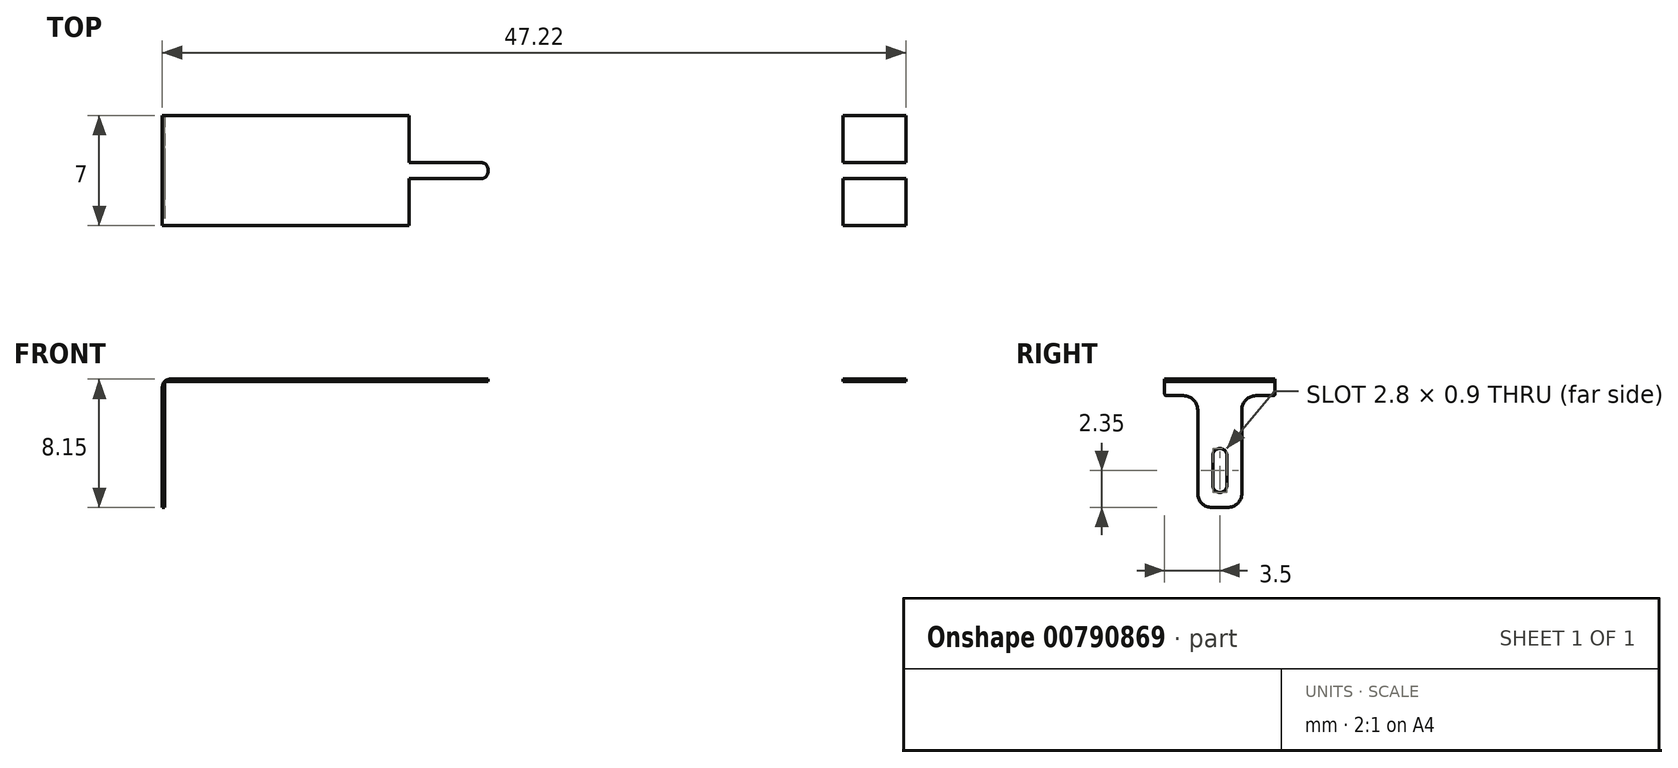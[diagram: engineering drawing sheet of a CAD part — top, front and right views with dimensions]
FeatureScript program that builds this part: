
annotation { "Feature Type Name" : "Feature", "Feature Type Description" : "" }
export const myFeature = defineFeature(function(context is Context, id is Id, definition is map)
    precondition{}
    {
        {
            var Q0;
            Q0=qCreatedBy(makeId("Top.planeOp"),FACE);
            var sketch = newSketch(context, id + "F0", { "sketchPlane" : qUnion([Q0])});
            skPoint(sketch, "E0.middle", {"position": v(0, 0) * mm});
            skLineSegment(sketch, "E1.bottom", {"start": v(-9.18, -0.5) * mm, "end": v(-13.77, -0.5) * mm});
            skLineSegment(sketch, "E1.top", {"start": v(-9.18, 0.5) * mm, "end": v(-13.77, 0.5) * mm});
            skLineSegment(sketch, "E1.left", {"start": v(-8.78, -0.1) * mm, "end": v(-8.78, 0.1) * mm});
            skLineSegment(sketch, "E1.right", {"start": v(-18.78, -0.1) * mm, "end": v(-18.78, 0.1) * mm});
            skPoint(sketch, "E1.middle", {"position": v(-13.78, 0) * mm});
            skPoint(sketch, "E2.visualSharp", {"position": v(-8.78, 0.5) * mm});
            skArc(sketch, "E2.filletArc", {"start": v(-8.78, 0.1) * mm, "mid": v(-8.9, 0.38) * mm, "end": v(-9.18, 0.5) * mm});
            skPoint(sketch, "E3.visualSharp", {"position": v(-8.78, -0.5) * mm});
            skArc(sketch, "E3.filletArc", {"start": v(-9.18, -0.5) * mm, "mid": v(-8.9, -0.38) * mm, "end": v(-8.78, -0.1) * mm});
            skPoint(sketch, "E4.visualSharp", {"position": v(-18.78, 0.5) * mm});
            skArc(sketch, "E4.filletArc", {"start": v(-18.38, 0.5) * mm, "mid": v(-18.66, 0.38) * mm, "end": v(-18.77, 0.1) * mm});
            skPoint(sketch, "E5.visualSharp", {"position": v(-18.78, -0.5) * mm});
            skArc(sketch, "E5.filletArc", {"start": v(-18.77, -0.1) * mm, "mid": v(-18.66, -0.38) * mm, "end": v(-18.38, -0.5) * mm});
            skLineSegment(sketch, "E6", {"start": v(0, 3.5) * mm, "end": v(-13.78, 3.5) * mm});
            skPoint(sketch, "E6.endSnap0", {"position": v(-13.77, 0.5) * mm});
            skLineSegment(sketch, "E7", {"start": v(-13.78, 3.5) * mm, "end": v(-13.78, 0.5) * mm});
            skLineSegment(sketch, "E8.MirrorCS", {"start": v(0, -3.5) * mm, "end": v(-13.78, -3.5) * mm});
            skLineSegment(sketch, "E9.MirrorCS", {"start": v(-13.78, -3.5) * mm, "end": v(-13.78, -0.5) * mm});
            skLineSegment(sketch, "E10.MirrorCS", {"start": v(0, 3.5) * mm, "end": v(13.78, 3.5) * mm});
            skLineSegment(sketch, "E11.MirrorCS", {"start": v(0, -3.5) * mm, "end": v(13.78, -3.5) * mm});
            skLineSegment(sketch, "E12.MirrorCS", {"start": v(8.78, -0.1) * mm, "end": v(8.78, 0.1) * mm});
            skArc(sketch, "E13.MirrorCS", {"start": v(8.78, 0.1) * mm, "mid": v(8.9, 0.38) * mm, "end": v(9.18, 0.5) * mm});
            skArc(sketch, "E14.MirrorCS", {"start": v(18.77, -0.1) * mm, "mid": v(18.66, -0.38) * mm, "end": v(18.38, -0.5) * mm});
            skLineSegment(sketch, "E15.MirrorCS", {"start": v(18.78, -0.1) * mm, "end": v(18.78, 0.1) * mm});
            skArc(sketch, "E16.MirrorCS", {"start": v(18.38, 0.5) * mm, "mid": v(18.66, 0.38) * mm, "end": v(18.77, 0.1) * mm});
            skArc(sketch, "E17.MirrorCS", {"start": v(9.18, -0.5) * mm, "mid": v(8.9, -0.38) * mm, "end": v(8.78, -0.1) * mm});
            skPoint(sketch, "E18.MirrorP", {"position": v(18.78, 0.5) * mm});
            skLineSegment(sketch, "E19.MirrorCS", {"start": v(9.18, 0.5) * mm, "end": v(18.38, 0.5) * mm});
            skLineSegment(sketch, "E20.MirrorCS", {"start": v(9.18, -0.5) * mm, "end": v(18.38, -0.5) * mm});
            skPoint(sketch, "E21.MirrorP", {"position": v(13.77, 0.5) * mm});
            skPoint(sketch, "E22.MirrorP", {"position": v(8.78, 0.5) * mm});
            skPoint(sketch, "E23.MirrorP", {"position": v(18.78, -0.5) * mm});
            skPoint(sketch, "E24.MirrorP", {"position": v(8.78, -0.5) * mm});
            skPoint(sketch, "E25.MirrorP", {"position": v(13.78, 0) * mm});
            skLineSegment(sketch, "E26.MirrorCS", {"start": v(13.78, 3.5) * mm, "end": v(13.78, 0.5) * mm});
            skLineSegment(sketch, "E27.MirrorCS", {"start": v(13.78, -3.5) * mm, "end": v(13.78, -0.5) * mm});
            skPoint(sketch, "E28.1.0.0", {"position": v(36.33, 0.5) * mm});
            skLineSegment(sketch, "E28.1.0.1", {"start": v(27.55, 3.5) * mm, "end": v(41.33, 3.5) * mm});
            skLineSegment(sketch, "E28.1.0.2", {"start": v(36.73, -0.5) * mm, "end": v(45.93, -0.5) * mm});
            skPoint(sketch, "E28.1.0.3", {"position": v(27.55, 0) * mm});
            skLineSegment(sketch, "E28.1.0.4", {"start": v(27.55, -3.5) * mm, "end": v(41.33, -3.5) * mm});
            skPoint(sketch, "E28.1.0.5", {"position": v(41.33, 0.5) * mm});
            skPoint(sketch, "E28.1.0.6", {"position": v(41.33, 0) * mm});
            skPoint(sketch, "E28.1.0.7", {"position": v(46.33, -0.5) * mm});
            skPoint(sketch, "E28.1.0.8", {"position": v(36.33, -0.5) * mm});
            skLineSegment(sketch, "E28.1.0.9", {"start": v(27.55, -3.5) * mm, "end": v(13.78, -3.5) * mm});
            skLineSegment(sketch, "E28.1.0.10", {"start": v(36.73, 0.5) * mm, "end": v(45.93, 0.5) * mm});
            skLineSegment(sketch, "E28.1.0.11", {"start": v(27.55, 3.5) * mm, "end": v(13.78, 3.5) * mm});
            skLineSegment(sketch, "E28.1.0.12", {"start": v(41.33, 3.5) * mm, "end": v(41.33, 0.5) * mm});
            skLineSegment(sketch, "E28.1.0.13", {"start": v(41.33, -3.5) * mm, "end": v(41.33, -0.5) * mm});
            skPoint(sketch, "E28.1.0.14", {"position": v(46.33, 0.5) * mm});
            skArc(sketch, "E28.1.0.15", {"start": v(45.93, 0.5) * mm, "mid": v(46.2, 0.38) * mm, "end": v(46.32, 0.1) * mm});
            skArc(sketch, "E28.1.0.16", {"start": v(36.73, -0.5) * mm, "mid": v(36.44, -0.38) * mm, "end": v(36.33, -0.1) * mm});
            skArc(sketch, "E28.1.0.17", {"start": v(46.33, -0.1) * mm, "mid": v(46.2, -0.38) * mm, "end": v(45.93, -0.5) * mm});
            skArc(sketch, "E28.1.0.18", {"start": v(36.33, 0.1) * mm, "mid": v(36.44, 0.38) * mm, "end": v(36.73, 0.5) * mm});
            skLineSegment(sketch, "E28.1.0.19", {"start": v(36.32, -0.1) * mm, "end": v(36.32, 0.1) * mm});
            skLineSegment(sketch, "E28.1.0.20", {"start": v(46.33, -0.1) * mm, "end": v(46.33, 0.1) * mm});
            skLineSegment(sketch, "E28.direction1", {"start": v(-13.78, -3.5) * mm, "end": v(13.78, -3.5) * mm, "construction": true});
            skLineSegment(sketch, "E29", {"start": v(0, 3.5) * mm, "end": v(0, -3.5) * mm});
            skLineSegment(sketch, "E30.bottom", {"start": v(96.43, -3.5) * mm, "end": v(99.43, -3.5) * mm});
            skLineSegment(sketch, "E30.top", {"start": v(96.43, 3.5) * mm, "end": v(99.43, 3.5) * mm});
            skLineSegment(sketch, "E30.left", {"start": v(96.43, -3.5) * mm, "end": v(96.43, 3.5) * mm});
            skLineSegment(sketch, "E31.bottom", {"start": v(41.33, -3.5) * mm, "end": v(45.33, -3.5) * mm});
            skLineSegment(sketch, "E31.top", {"start": v(41.33, 3.5) * mm, "end": v(45.33, 3.5) * mm});
            skLineSegment(sketch, "E31.left", {"start": v(41.33, -3.5) * mm, "end": v(41.33, 3.5) * mm});
            skLineSegment(sketch, "E31.right", {"start": v(45.33, -3.5) * mm, "end": v(45.33, 3.5) * mm});
            skSolve(sketch);
        }
        {
            var Q0;
            {var subQ8=sQuery(id+"F0.wireOp",EDGE,"E28.3.0.12");Q0=makeQuery(id+"F0.imprint","IMPRINT",FACE,{"disambiguationData":[TD([[makeQuery(id+"F0.imprint","IMPRINT",EDGE,{"derivedFrom":subQ8}),1.0]])]});}
            var Q1;
            {var subQ3=sQuery(id+"F0.wireOp",EDGE,"E14.MirrorCS");Q1=makeQuery(id+"F0.imprint","IMPRINT",FACE,{"disambiguationData":[TD([[makeQuery(id+"F0.imprint","IMPRINT",EDGE,{"derivedFrom":subQ3}),1.0]])]});}
            var Q2;
            {var subQ8=sQuery(id+"F0.wireOp",EDGE,"E28.1.0.12");Q2=makeQuery(id+"F0.imprint","IMPRINT",FACE,{"disambiguationData":[TD([[makeQuery(id+"F0.imprint","IMPRINT",EDGE,{"derivedFrom":subQ8}),1.0]])]});}
            var Q3;
            {var subQ8=sQuery(id+"F0.wireOp",EDGE,"E28.2.0.12");Q3=makeQuery(id+"F0.imprint","IMPRINT",FACE,{"disambiguationData":[TD([[makeQuery(id+"F0.imprint","IMPRINT",EDGE,{"derivedFrom":subQ8}),1.0]])]});}
            var Q4;
            Q4=makeQuery(id+"F0.imprint","IMPRINT",FACE,{"disambiguationData":[TD([[makeQuery(id+"F0.imprint","IMPRINT",EDGE,{"derivedFrom":sQuery(id+"F0.wireOp",EDGE,"E10.MirrorCS")}),-1.0]])]});
            var Q5;
            {var subQ5=sQuery(id+"F0.wireOp",EDGE,"E30.top");Q5=makeQuery(id+"F0.imprint","IMPRINT",FACE,{"disambiguationData":[TD([[makeQuery(id+"F0.imprint","IMPRINT",EDGE,{"derivedFrom":subQ5}),-1.0]])]});}
            var Q6;
            {var subQ5=sQuery(id+"F0.wireOp",EDGE,"E30.bottom");Q6=makeQuery(id+"F0.imprint","IMPRINT",FACE,{"disambiguationData":[TD([[makeQuery(id+"F0.imprint","IMPRINT",EDGE,{"derivedFrom":subQ5}),1.0]])]});}
            var Q7;
            {var subQ11=sQuery(id+"F0.wireOp",EDGE,"E28.3.0.15");Q7=makeQuery(id+"F0.imprint","IMPRINT",FACE,{"disambiguationData":[TD([[makeQuery(id+"F0.imprint","IMPRINT",EDGE,{"derivedFrom":subQ11}),1.0]])]});}
            var Q8;
            {var subQ5=sQuery(id+"F0.wireOp",EDGE,"E31.top");Q8=makeQuery(id+"F0.imprint","IMPRINT",FACE,{"disambiguationData":[TD([[makeQuery(id+"F0.imprint","IMPRINT",EDGE,{"derivedFrom":subQ5}),-1.0]])]});}
            var Q9;
            {var subQ5=sQuery(id+"F0.wireOp",EDGE,"E31.bottom");Q9=makeQuery(id+"F0.imprint","IMPRINT",FACE,{"disambiguationData":[TD([[makeQuery(id+"F0.imprint","IMPRINT",EDGE,{"derivedFrom":subQ5}),1.0]])]});}
            extrude(context, id + "F1", {"entities" : qUnion([Q0, Q1, Q2, Q3, Q4, Q5, Q6, Q7, Q8, Q9]), "depth" : 0.15 * mm, "offsetDistance" : 25 * mm});
        }
        {
            var Q0;
            Q0=makeQuery(id+"F1.opExtrude","SWEPT_FACE",FACE,{"disambiguationData":[OSD([sQuery(id+"F0.wireOp",EDGE,"E29")])]});
            extrude(context, id + "F2", {"entities" : qUnion([Q0]), "operationType" : NewBodyOperationType.ADD, "depth" : 1.9 * mm, "offsetDistance" : 25 * mm});
        }
        {
            var Q0;
            {var subQ0=sQuery(id+"F0.wireOp",EDGE,"E29");Q0=makeQuery(id+"F2.boolean.opBoolean","MERGE",FACE,{"derivedFrom":[makeQuery(id+"F1.opExtrude","CAP_FACE",FACE,{"disambiguationData":[OSD([sQuery(id+"F0.wireOp",EDGE,"E10.MirrorCS"),sQuery(id+"F0.wireOp",EDGE,"E11.MirrorCS"),sQuery(id+"F0.wireOp",EDGE,"E12.MirrorCS"),sQuery(id+"F0.wireOp",EDGE,"E13.MirrorCS"),sQuery(id+"F0.wireOp",EDGE,"E14.MirrorCS"),sQuery(id+"F0.wireOp",EDGE,"E15.MirrorCS"),sQuery(id+"F0.wireOp",EDGE,"E16.MirrorCS"),sQuery(id+"F0.wireOp",EDGE,"E17.MirrorCS"),sQuery(id+"F0.wireOp",EDGE,"E19.MirrorCS"),sQuery(id+"F0.wireOp",EDGE,"E20.MirrorCS"),sQuery(id+"F0.wireOp",EDGE,"E28.1.0.1"),sQuery(id+"F0.wireOp",EDGE,"E28.1.0.2"),sQuery(id+"F0.wireOp",EDGE,"E28.1.0.4"),sQuery(id+"F0.wireOp",EDGE,"E28.1.0.9"),sQuery(id+"F0.wireOp",EDGE,"E28.1.0.10"),sQuery(id+"F0.wireOp",EDGE,"E28.1.0.11"),sQuery(id+"F0.wireOp",EDGE,"E28.1.0.15"),sQuery(id+"F0.wireOp",EDGE,"E28.1.0.16"),sQuery(id+"F0.wireOp",EDGE,"E28.1.0.17"),sQuery(id+"F0.wireOp",EDGE,"E28.1.0.18"),sQuery(id+"F0.wireOp",EDGE,"E28.1.0.19"),sQuery(id+"F0.wireOp",EDGE,"E28.1.0.20"),sQuery(id+"F0.wireOp",EDGE,"E28.2.0.1"),sQuery(id+"F0.wireOp",EDGE,"E28.2.0.2"),sQuery(id+"F0.wireOp",EDGE,"E28.2.0.4"),sQuery(id+"F0.wireOp",EDGE,"E28.2.0.9"),sQuery(id+"F0.wireOp",EDGE,"E28.2.0.10"),sQuery(id+"F0.wireOp",EDGE,"E28.2.0.11"),sQuery(id+"F0.wireOp",EDGE,"E28.2.0.15"),sQuery(id+"F0.wireOp",EDGE,"E28.2.0.16"),sQuery(id+"F0.wireOp",EDGE,"E28.2.0.17"),sQuery(id+"F0.wireOp",EDGE,"E28.2.0.18"),sQuery(id+"F0.wireOp",EDGE,"E28.2.0.19"),sQuery(id+"F0.wireOp",EDGE,"E28.2.0.20"),sQuery(id+"F0.wireOp",EDGE,"E28.3.0.1"),sQuery(id+"F0.wireOp",EDGE,"E28.3.0.2"),sQuery(id+"F0.wireOp",EDGE,"E28.3.0.4"),sQuery(id+"F0.wireOp",EDGE,"E28.3.0.9"),sQuery(id+"F0.wireOp",EDGE,"E28.3.0.10"),sQuery(id+"F0.wireOp",EDGE,"E28.3.0.11"),sQuery(id+"F0.wireOp",EDGE,"E28.3.0.12"),sQuery(id+"F0.wireOp",EDGE,"E28.3.0.13"),sQuery(id+"F0.wireOp",EDGE,"E28.3.0.16"),sQuery(id+"F0.wireOp",EDGE,"E28.3.0.18"),sQuery(id+"F0.wireOp",EDGE,"E28.3.0.19"),subQ0])],"isStart":true}),makeQuery(id+"F2.opExtrude","SWEPT_FACE",FACE,{"disambiguationData":[OSD([subQ0]),TDD([makeQuery(id+"F1.opExtrude","CAP_EDGE",EDGE,{"disambiguationData":[OSD([subQ0])],"isStart":true})])]})]});}
            var sketch = newSketch(context, id + "F3", { "sketchPlane" : qUnion([Q0])});
            skLineSegment(sketch, "E32.bottom", {"start": v(-1.9, -3.5) * mm, "end": v(-1.75, -3.5) * mm});
            skLineSegment(sketch, "E32.top", {"start": v(-1.9, 3.5) * mm, "end": v(-1.75, 3.5) * mm});
            skLineSegment(sketch, "E32.left", {"start": v(-1.9, -3.5) * mm, "end": v(-1.9, 3.5) * mm});
            skLineSegment(sketch, "E32.right", {"start": v(-1.75, -3.5) * mm, "end": v(-1.75, 3.5) * mm});
            skSolve(sketch);
        }
        {
            var Q0;
            Q0=qSketchRegion(id+"F3",true);
            extrude(context, id + "F4", {"entities" : qUnion([Q0]), "operationType" : NewBodyOperationType.ADD, "depth" : 8 * mm, "offsetDistance" : 25 * mm});
        }
        {
            var Q0;
            Q0=makeQuery(id+"F4.boolean.opBoolean","MERGE",FACE,{"derivedFrom":[makeQuery(id+"F2.opExtrude","CAP_FACE",FACE,{"disambiguationData":[OSD([sQuery(id+"F0.wireOp",EDGE,"E29")])],"isStart":false}),makeQuery(id+"F4.opExtrude","SWEPT_FACE",FACE,{"disambiguationData":[OSD([sQuery(id+"F3.wireOp",EDGE,"E32.left")])]})]});
            var sketch = newSketch(context, id + "F5", { "sketchPlane" : qUnion([Q0])});
            skPoint(sketch, "E33.middle.positionSnap0", {"position": v(0, -8) * mm});
            skLineSegment(sketch, "E34.bottom", {"start": v(-0.5, -8) * mm, "end": v(0.5, -8) * mm});
            skLineSegment(sketch, "E34.top", {"start": v(-1.4, -0.9) * mm, "end": v(1.4, -0.9) * mm});
            skLineSegment(sketch, "E34.left", {"start": v(-1.4, -7.1) * mm, "end": v(-1.4, -1.8) * mm});
            skLineSegment(sketch, "E34.right", {"start": v(1.4, -7.1) * mm, "end": v(1.4, -1.8) * mm});
            skLineSegment(sketch, "E35", {"start": v(2.3, -0.9) * mm, "end": v(3.4, -0.9) * mm});
            skLineSegment(sketch, "E36", {"start": v(-2.3, -0.9) * mm, "end": v(-3.4, -0.9) * mm});
            skCircle(sketch, "E37", {"center": v(0, -6.6) * mm, "radius": 0.45 * mm});
            skCircle(sketch, "E38", {"center": v(0, -4.7) * mm, "radius": 0.45 * mm});
            skLineSegment(sketch, "E39", {"start": v(0.45, -4.7) * mm, "end": v(0.45, -6.6) * mm});
            skLineSegment(sketch, "E40", {"start": v(-0.45, -4.7) * mm, "end": v(-0.45, -6.6) * mm});
            skPoint(sketch, "E41.visualSharp", {"position": v(-1.4, -8) * mm});
            skArc(sketch, "E41.filletArc", {"start": v(-1.4, -7.1) * mm, "mid": v(-1.14, -7.74) * mm, "end": v(-0.5, -8) * mm});
            skPoint(sketch, "E42.visualSharp", {"position": v(1.4, -8) * mm});
            skArc(sketch, "E42.filletArc", {"start": v(0.5, -8) * mm, "mid": v(1.14, -7.74) * mm, "end": v(1.4, -7.1) * mm});
            skPoint(sketch, "E43.visualSharp", {"position": v(-1.4, -0.9) * mm});
            skArc(sketch, "E43.filletArc", {"start": v(-1.4, -1.8) * mm, "mid": v(-1.66, -1.16) * mm, "end": v(-2.3, -0.9) * mm});
            skPoint(sketch, "E44.visualSharp", {"position": v(1.4, -0.9) * mm});
            skArc(sketch, "E44.filletArc", {"start": v(2.3, -0.9) * mm, "mid": v(1.66, -1.16) * mm, "end": v(1.4, -1.8) * mm});
            skLineSegment(sketch, "E45", {"start": v(-3.5, -0.8) * mm, "end": v(-3.5, 0.15) * mm});
            skLineSegment(sketch, "E46", {"start": v(3.5, -0.8) * mm, "end": v(3.5, 0.15) * mm});
            skPoint(sketch, "E47.visualSharp", {"position": v(-3.5, -0.9) * mm});
            skArc(sketch, "E47.filletArc", {"start": v(-3.5, -0.8) * mm, "mid": v(-3.47, -0.87) * mm, "end": v(-3.4, -0.9) * mm});
            skPoint(sketch, "E48.visualSharp", {"position": v(3.5, -0.9) * mm});
            skArc(sketch, "E48.filletArc", {"start": v(3.4, -0.9) * mm, "mid": v(3.47, -0.87) * mm, "end": v(3.5, -0.8) * mm});
            skSolve(sketch);
        }
        {
            var Q0;
            Q0=makeQuery(id+"F5.imprint","IMPRINT",FACE,{"disambiguationData":[TD([[makeQuery(id+"F5.imprint","IMPRINT",EDGE,{"derivedFrom":sQuery(id+"F5.wireOp",EDGE,"E34.left")}),1.0]])]});
            var Q1;
            Q1=makeQuery(id+"F5.imprint","IMPRINT",FACE,{"disambiguationData":[TD([[makeQuery(id+"F5.imprint","IMPRINT",EDGE,{"derivedFrom":sQuery(id+"F5.wireOp",EDGE,"E34.right")}),-1.0]])]});
            var Q2;
            {var subQ0=sQuery(id+"F5.wireOp",EDGE,"E37");var subQ1=makeQuery(id+"F5.imprint","INTERSECT",VERTEX,{"derivedFrom":[subQ0,sQuery(id+"F5.wireOp",EDGE,"E39")]});Q2=makeQuery(id+"F5.imprint","IMPRINT",FACE,{"disambiguationData":[TD([[makeQuery(id+"F5.imprint","IMPRINT",EDGE,{"disambiguationData":[TD([[subQ1,-1.0]])],"derivedFrom":subQ0}),1.0]])]});}
            var Q3;
            {var subQ0=sQuery(id+"F5.wireOp",EDGE,"E39");Q3=makeQuery(id+"F5.imprint","IMPRINT",FACE,{"disambiguationData":[TD([[makeQuery(id+"F5.imprint","IMPRINT",EDGE,{"derivedFrom":subQ0}),-1.0]])]});}
            var Q4;
            {var subQ0=sQuery(id+"F5.wireOp",EDGE,"E38");var subQ1=makeQuery(id+"F5.imprint","INTERSECT",VERTEX,{"derivedFrom":[subQ0,sQuery(id+"F5.wireOp",EDGE,"E39")]});Q4=makeQuery(id+"F5.imprint","IMPRINT",FACE,{"disambiguationData":[TD([[makeQuery(id+"F5.imprint","IMPRINT",EDGE,{"disambiguationData":[TD([[subQ1,-1.0]])],"derivedFrom":subQ0}),1.0]])]});}
            extrude(context, id + "F6", {"entities" : qUnion([Q0, Q1, Q2, Q3, Q4]), "operationType" : NewBodyOperationType.REMOVE, "oppositeDirection" : true, "depth" : 25 * mm, "offsetDistance" : 25 * mm});
        }
        {
            var Q0;
            {var subQ0=sQuery(id+"F0.wireOp",EDGE,"E29");Q0=makeQuery(id+"F2.opExtrude","CAP_EDGE",EDGE,{"disambiguationData":[OSD([subQ0]),TDD([makeQuery(id+"F1.opExtrude","CAP_EDGE",EDGE,{"disambiguationData":[OSD([subQ0])],"isStart":false})])],"isStart":false});}
            var Q1;
            Q1=makeQuery(id+"F4.opExtrude","CAP_EDGE",EDGE,{"disambiguationData":[OSD([sQuery(id+"F3.wireOp",EDGE,"E32.right")])],"isStart":true});
            fillet(context, id + "F7", {"entities" : qUnion([Q0, Q1]), "radius" : 0.5 * mm, "tangentPropagation" : true, "allowEdgeOverflow" : false});
        }
    });
